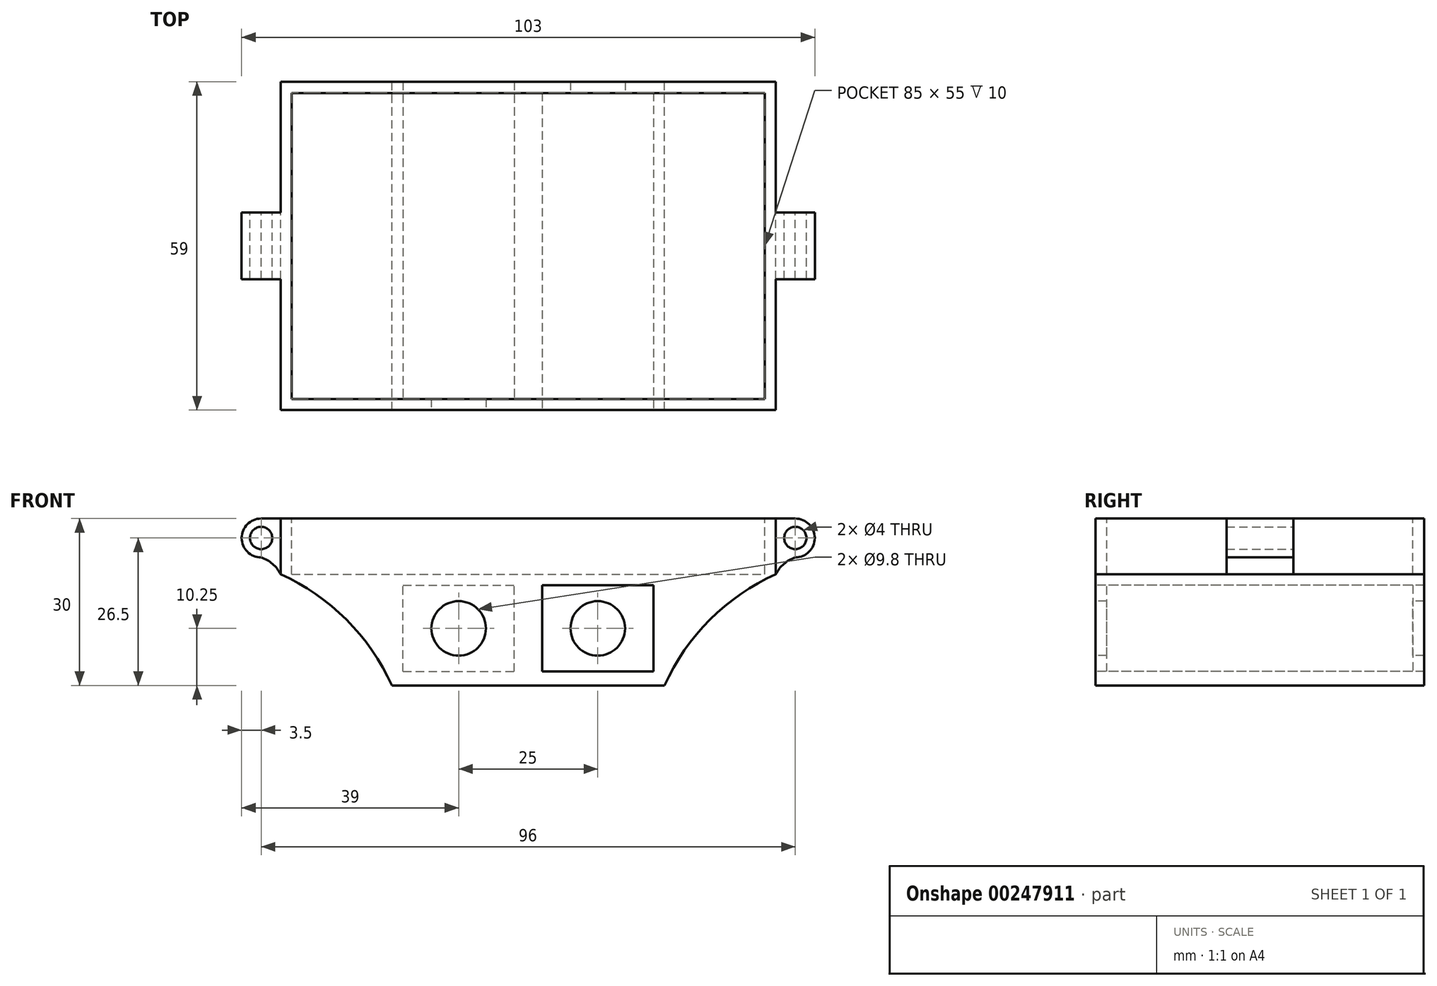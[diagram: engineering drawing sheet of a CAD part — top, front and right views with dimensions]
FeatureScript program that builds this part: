
annotation { "Feature Type Name" : "Feature", "Feature Type Description" : "" }
export const myFeature = defineFeature(function(context is Context, id is Id, definition is map)
    precondition{}
    {
        {
            var Q0;
            Q0=qCreatedBy(makeId("Front.planeOp"),FACE);
            var sketch = newSketch(context, id + "F0", { "sketchPlane" : qUnion([Q0])});
            skLineSegment(sketch, "E0.bottom", {"start": v(-44.5, 15) * mm, "end": v(44.5, 15) * mm});
            skLineSegment(sketch, "E0.top", {"start": v(-24.5, -15) * mm, "end": v(24.5, -15) * mm});
            skLineSegment(sketch, "E0.left", {"start": v(-44.5, 15) * mm, "end": v(-44.5, 5) * mm});
            skLineSegment(sketch, "E0.right", {"start": v(44.5, 15) * mm, "end": v(44.5, 5) * mm});
            skPoint(sketch, "E0.middle", {"position": v(0, 0) * mm});
            skArc(sketch, "E1", {"start": v(-24.5, -15) * mm, "mid": v(-32.67, -3.17) * mm, "end": v(-44.5, 5) * mm});
            skLineSegment(sketch, "E2", {"start": v(0, 0) * mm, "end": v(0, -15) * mm});
            skArc(sketch, "E3.MirrorCS", {"start": v(24.5, -15) * mm, "mid": v(32.67, -3.17) * mm, "end": v(44.5, 5) * mm});
            skPoint(sketch, "E4.orphan", {"position": v(-44.5, -15) * mm});
            skPoint(sketch, "E5.orphan", {"position": v(44.5, -15) * mm});
            skSolve(sketch);
        }
        {
            var Q0;
            Q0 = qSketchRegion(id + "F0", true);
            extrude(context, id + "F1", {"entities" : qUnion([Q0]), "depth" : 59 / 2 * mm, "hasSecondDirection" : true, "secondDirectionOppositeDirection" : true, "secondDirectionDepth" : 29.5 * mm});
        }
        {
            var Q0;
            Q0=qCreatedBy(makeId("Front.planeOp"),FACE);
            var sketch = newSketch(context, id + "F2", { "sketchPlane" : qUnion([Q0])});
            skLineSegment(sketch, "E6.0", {"start": v(-44.5, 15) * mm, "end": v(44.5, 15) * mm});
            skLineSegment(sketch, "E7.0", {"start": v(-44.5, 15) * mm, "end": v(-44.5, 5) * mm});
            skLineSegment(sketch, "E8", {"start": v(-44.5, 15) * mm, "end": v(-48, 15) * mm});
            skArc(sketch, "E9", {"start": v(-48, 15) * mm, "mid": v(-51.5, 11.5) * mm, "end": v(-48, 8) * mm});
            skCircle(sketch, "E10", {"center": v(-48, 11.5) * mm, "radius": 2 * mm});
            skArc(sketch, "E11", {"start": v(-44.5, 5) * mm, "mid": v(-45.95, 6.85) * mm, "end": v(-48, 8) * mm});
            skLineSegment(sketch, "E12", {"start": v(0, 0) * mm, "end": v(0, 15) * mm});
            skArc(sketch, "E13.MirrorCS", {"start": v(48, 15) * mm, "mid": v(51.5, 11.5) * mm, "end": v(48, 8) * mm});
            skCircle(sketch, "E14.MirrorC", {"center": v(48, 11.5) * mm, "radius": 2 * mm});
            skLineSegment(sketch, "E15.MirrorCS", {"start": v(44.5, 15) * mm, "end": v(48, 15) * mm});
            skArc(sketch, "E16.MirrorCS", {"start": v(44.5, 5) * mm, "mid": v(45.95, 6.85) * mm, "end": v(48, 8) * mm});
            skLineSegment(sketch, "E17.MirrorCS", {"start": v(44.5, 15) * mm, "end": v(44.5, 5) * mm});
            skSolve(sketch);
        }
        {
            var Q0;
            Q0 = qSketchRegion(id + "F2", true);
            extrude(context, id + "F3", {"entities" : qUnion([Q0]), "operationType" : NewBodyOperationType.ADD, "depth" : 6 * mm, "hasSecondDirection" : true, "secondDirectionOppositeDirection" : true, "secondDirectionDepth" : 6 * mm});
        }
        {
            var Q0;
            Q0=makeQuery(id+"F3.boolean.opBoolean","MERGE",FACE,{"derivedFrom":[makeQuery(id+"F1.opExtrude","SWEPT_FACE",FACE,{"disambiguationData":[OSD([sQuery(id+"F0.wireOp",EDGE,"E0.bottom")])]}),makeQuery(id+"F3.opExtrude","SWEPT_FACE",FACE,{"disambiguationData":[OSD([sQuery(id+"F2.wireOp",EDGE,"E8")])]}),makeQuery(id+"F3.opExtrude","SWEPT_FACE",FACE,{"disambiguationData":[OSD([sQuery(id+"F2.wireOp",EDGE,"E15.MirrorCS")])]})]});
            var sketch = newSketch(context, id + "F4", { "sketchPlane" : qUnion([Q0])});
            skLineSegment(sketch, "E18.bottom", {"start": v(-42.5, 27.5) * mm, "end": v(42.5, 27.5) * mm});
            skLineSegment(sketch, "E18.top", {"start": v(-42.5, -27.5) * mm, "end": v(42.5, -27.5) * mm});
            skLineSegment(sketch, "E18.left", {"start": v(-42.5, 27.5) * mm, "end": v(-42.5, -27.5) * mm});
            skLineSegment(sketch, "E18.right", {"start": v(42.5, 27.5) * mm, "end": v(42.5, -27.5) * mm});
            skPoint(sketch, "E18.middle", {"position": v(0, 0) * mm});
            skSolve(sketch);
        }
        {
            var Q0;
            Q0 = qSketchRegion(id + "F4", true);
            extrude(context, id + "F5", {"entities" : qUnion([Q0]), "operationType" : NewBodyOperationType.REMOVE, "oppositeDirection" : true, "depth" : 10 * mm});
        }
        {
            var Q0;
            Q0=qCreatedBy(makeId("Front.planeOp"),FACE);
            var sketch = newSketch(context, id + "F6", { "sketchPlane" : qUnion([Q0])});
            skLineSegment(sketch, "E19.bottom", {"start": v(-22.5, -12.5) * mm, "end": v(-2.5, -12.5) * mm});
            skLineSegment(sketch, "E19.top", {"start": v(-22.5, 3) * mm, "end": v(-2.5, 3) * mm});
            skLineSegment(sketch, "E19.left", {"start": v(-22.5, -12.5) * mm, "end": v(-22.5, 3) * mm});
            skLineSegment(sketch, "E19.right", {"start": v(-2.5, -12.5) * mm, "end": v(-2.5, 3) * mm});
            skSolve(sketch);
        }
        {
            var Q0;
            Q0 = qSketchRegion(id + "F6", true);
            extrude(context, id + "F7", {"entities" : qUnion([Q0]), "operationType" : NewBodyOperationType.REMOVE, "oppositeDirection" : true, "depth" : (59 / 2) * mm, "hasSecondDirection" : true, "secondDirectionOppositeDirection" : false, "secondDirectionDepth" : (29.5 - 2) * mm});
        }
        {
            var Q0;
            Q0=makeQuery(id+"F1.opExtrude","CAP_FACE",FACE,{"disambiguationData":[OSD([sQuery(id+"F0.wireOp",EDGE,"E0.bottom"),sQuery(id+"F0.wireOp",EDGE,"E0.top"),sQuery(id+"F0.wireOp",EDGE,"E0.right"),sQuery(id+"F0.wireOp",EDGE,"E0.left"),sQuery(id+"F0.wireOp",EDGE,"E1"),sQuery(id+"F0.wireOp",EDGE,"E3.MirrorCS")])],"isStart":false});
            var sketch = newSketch(context, id + "F8", { "sketchPlane" : qUnion([Q0])});
            skLineSegment(sketch, "E20.bottom", {"start": v(2.5, 3) * mm, "end": v(22.5, 3) * mm});
            skLineSegment(sketch, "E20.top", {"start": v(2.5, -12.5) * mm, "end": v(22.5, -12.5) * mm});
            skLineSegment(sketch, "E20.left", {"start": v(2.5, 3) * mm, "end": v(2.5, -12.5) * mm});
            skLineSegment(sketch, "E20.right", {"start": v(22.5, 3) * mm, "end": v(22.5, -12.5) * mm});
            skSolve(sketch);
        }
        {
            var Q0;
            Q0 = qSketchRegion(id + "F8", true);
            extrude(context, id + "F9", {"entities" : qUnion([Q0]), "operationType" : NewBodyOperationType.REMOVE, "oppositeDirection" : true, "depth" : 57 * mm});
        }
        {
            var Q0;
            Q0=qCreatedBy(makeId("Front.planeOp"),FACE);
            var sketch = newSketch(context, id + "F10", { "sketchPlane" : qUnion([Q0])});
            skLineSegment(sketch, "E21.0.0", {"start": v(2.5, 3) * mm, "end": v(2.5, -12.5) * mm});
            skLineSegment(sketch, "E21.0.1", {"start": v(2.5, -12.5) * mm, "end": v(22.5, -12.5) * mm});
            skLineSegment(sketch, "E21.0.2", {"start": v(22.5, -12.5) * mm, "end": v(22.5, 3) * mm});
            skLineSegment(sketch, "E21.0.3", {"start": v(22.5, 3) * mm, "end": v(2.5, 3) * mm});
            skLineSegment(sketch, "E22.0.0", {"start": v(-2.5, 3) * mm, "end": v(-22.5, 3) * mm});
            skLineSegment(sketch, "E22.0.1", {"start": v(-22.5, 3) * mm, "end": v(-22.5, -12.5) * mm});
            skLineSegment(sketch, "E22.0.2", {"start": v(-22.5, -12.5) * mm, "end": v(-2.5, -12.5) * mm});
            skLineSegment(sketch, "E22.0.3", {"start": v(-2.5, -12.5) * mm, "end": v(-2.5, 3) * mm});
            skCircle(sketch, "E23", {"center": v(12.5, -4.75) * mm, "radius": 4.9 * mm});
            skPoint(sketch, "E23.centerSnap0", {"position": v(22.5, -4.75) * mm});
            skPoint(sketch, "E23.centerSnap1", {"position": v(12.5, 3) * mm});
            skCircle(sketch, "E24", {"center": v(-12.5, -4.75) * mm, "radius": 4.9 * mm});
            skPoint(sketch, "E24.centerSnap0", {"position": v(-2.5, -4.75) * mm});
            skPoint(sketch, "E24.centerSnap1", {"position": v(-12.5, 3) * mm});
            skSolve(sketch);
        }
        {
            var Q0;
            Q0=makeQuery(id+"F10.imprint","IMPRINT",FACE,{"disambiguationData":[TD([[makeQuery(id+"F10.imprint","IMPRINT",EDGE,{"derivedFrom":sQuery(id+"F10.wireOp",EDGE,"E24")}),1.0]])]});
            var Q1;
            Q1=makeQuery(id+"F10.imprint","IMPRINT",FACE,{"disambiguationData":[TD([[makeQuery(id+"F10.imprint","IMPRINT",EDGE,{"derivedFrom":sQuery(id+"F10.wireOp",EDGE,"E23")}),1.0]])]});
            extrude(context, id + "F11", {"entities" : qUnion([Q0, Q1]), "operationType" : NewBodyOperationType.REMOVE, "oppositeDirection" : true, "depth" : 80 * mm, "hasSecondDirection" : true, "secondDirectionOppositeDirection" : false, "secondDirectionDepth" : 80 * mm});
        }
    });
